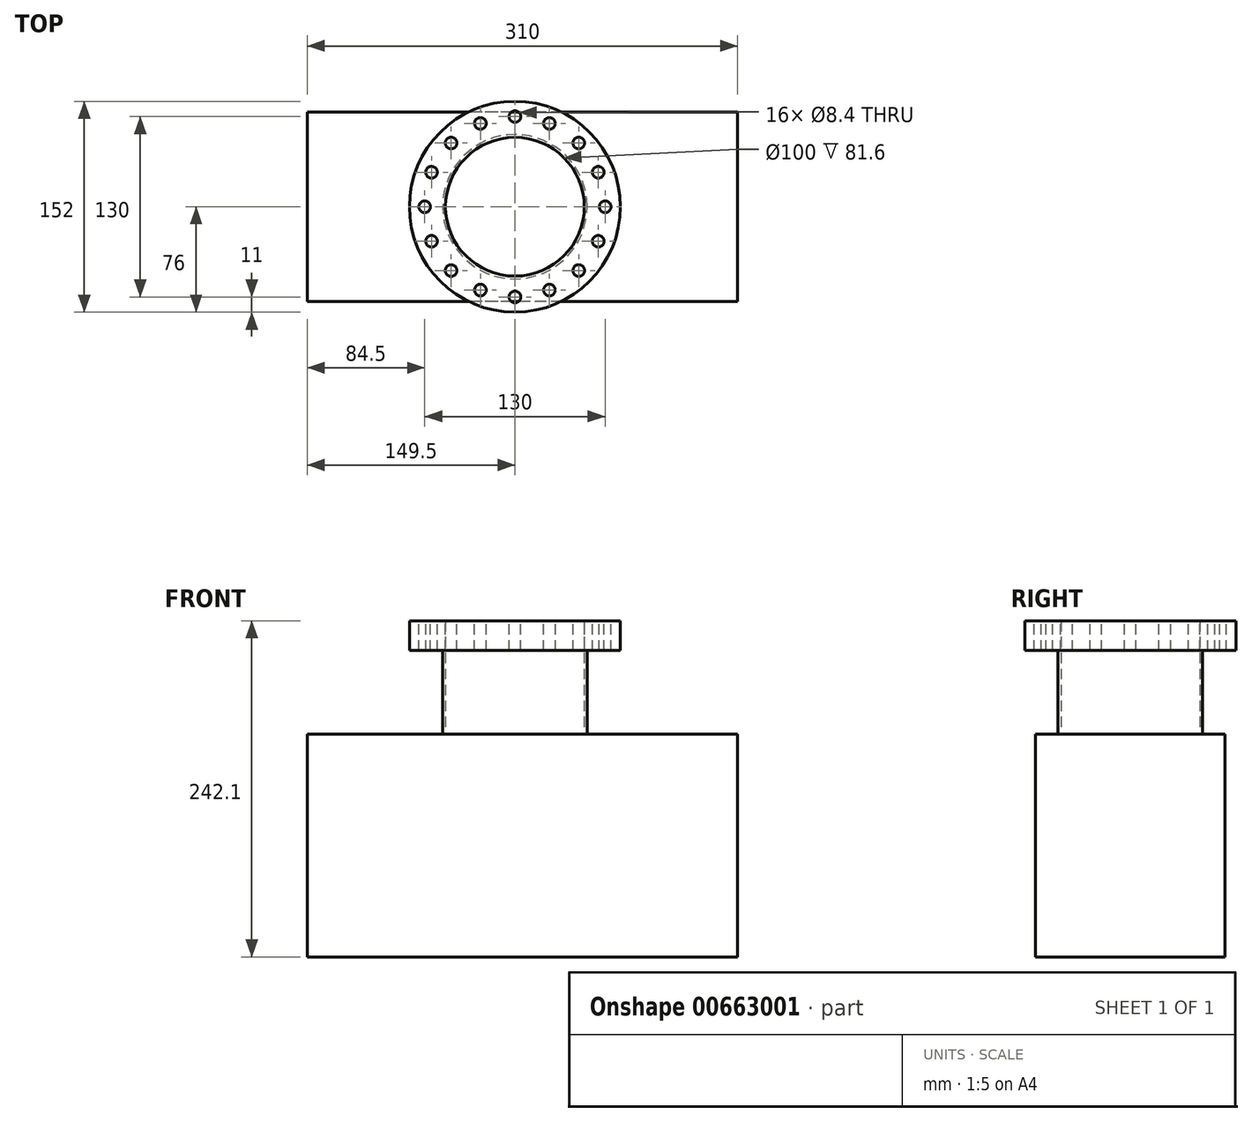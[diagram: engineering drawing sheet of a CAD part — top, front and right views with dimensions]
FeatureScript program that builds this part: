
annotation { "Feature Type Name" : "Feature", "Feature Type Description" : "" }
export const myFeature = defineFeature(function(context is Context, id is Id, definition is map)
    precondition{}
    {
        {
            var Q0;
            Q0=qCreatedBy(makeId("Top.planeOp"),FACE);
            var sketch = newSketch(context, id + "F0", { "sketchPlane" : qUnion([Q0])});
            skLineSegment(sketch, "E0.bottom", {"start": v(155, -68.25) * mm, "end": v(-155, -68.25) * mm});
            skLineSegment(sketch, "E0.top", {"start": v(155, 68.25) * mm, "end": v(-155, 68.25) * mm});
            skLineSegment(sketch, "E0.left", {"start": v(155, -68.25) * mm, "end": v(155, 68.25) * mm});
            skLineSegment(sketch, "E0.right", {"start": v(-155, -68.25) * mm, "end": v(-155, 68.25) * mm});
            skPoint(sketch, "E0.middle", {"position": v(0, 0) * mm});
            skSolve(sketch);
        }
        {
            var Q0;
            Q0=makeQuery(id+"F0.imprint","IMPRINT",FACE,{"disambiguationData":[TD([[makeQuery(id+"F0.imprint","IMPRINT",EDGE,{"derivedFrom":sQuery(id+"F0.wireOp",EDGE,"E0.bottom")}),-1.0]])]});
            extrude(context, id + "F1", {"entities" : qUnion([Q0]), "depth" : (242.1 - 81.6) * mm, "offsetDistance" : 25 * mm});
        }
        {
            var Q0;
            Q0=makeQuery(id+"F1.opExtrude","CAP_FACE",FACE,{"disambiguationData":[OSD([sQuery(id+"F0.wireOp",EDGE,"E0.bottom"),sQuery(id+"F0.wireOp",EDGE,"E0.top"),sQuery(id+"F0.wireOp",EDGE,"E0.left"),sQuery(id+"F0.wireOp",EDGE,"E0.right")])],"isStart":false});
            var sketch = newSketch(context, id + "F2", { "sketchPlane" : qUnion([Q0])});
            skCircle(sketch, "E1", {"center": v(-5.5, 0) * mm, "radius": 50 * mm});
            skCircle(sketch, "E2.0", {"center": v(-5.5, 0) * mm, "radius": 52 * mm});
            skCircle(sketch, "E3", {"center": v(-5.5, 0) * mm, "radius": 76 * mm});
            skSolve(sketch);
        }
        {
            var Q0;
            Q0=makeQuery(id+"F2.imprint","IMPRINT",FACE,{"disambiguationData":[TD([[makeQuery(id+"F2.imprint","IMPRINT",EDGE,{"derivedFrom":sQuery(id+"F2.wireOp",EDGE,"E1")}),-1.0]])]});
            extrude(context, id + "F3", {"entities" : qUnion([Q0]), "operationType" : NewBodyOperationType.ADD, "depth" : (81.6 - 21.3) * mm, "offsetDistance" : 25 * mm});
        }
        {
            var Q0;
            Q0=makeQuery(id+"F3.opExtrude","CAP_FACE",FACE,{"disambiguationData":[OSD([sQuery(id+"F2.wireOp",EDGE,"E1"),sQuery(id+"F2.wireOp",EDGE,"E2.0")])],"isStart":false});
            var sketch = newSketch(context, id + "F4", { "sketchPlane" : qUnion([Q0])});
            skCircle(sketch, "E4", {"center": v(-5.5, 0) * mm, "radius": 76 * mm});
            skSolve(sketch);
        }
        {
            var Q0;
            Q0=makeQuery(id+"F4.imprint","IMPRINT",FACE,{"disambiguationData":[TD([[makeQuery(id+"F4.imprint","IMPRINT",EDGE,{"derivedFrom":makeQuery(id+"F3.opExtrude","CAP_EDGE",EDGE,{"disambiguationData":[OSD([sQuery(id+"F2.wireOp",EDGE,"E1")])],"isStart":false})}),-1.0]])]});
            var Q1;
            Q1=makeQuery(id+"F4.imprint","IMPRINT",FACE,{"disambiguationData":[TD([[makeQuery(id+"F4.imprint","IMPRINT",EDGE,{"derivedFrom":sQuery(id+"F4.wireOp",EDGE,"E4")}),1.0]])]});
            extrude(context, id + "F5", {"entities" : qUnion([Q0, Q1]), "operationType" : NewBodyOperationType.ADD, "depth" : 21.3 * mm, "offsetDistance" : 25 * mm});
        }
        {
            var Q0;
            Q0=makeQuery(id+"F5.opExtrude","CAP_FACE",FACE,{"disambiguationData":[OSD([sQuery(id+"F2.wireOp",EDGE,"E1"),sQuery(id+"F4.wireOp",EDGE,"E4")])],"isStart":false});
            var sketch = newSketch(context, id + "F6", { "sketchPlane" : qUnion([Q0])});
            skCircle(sketch, "E5", {"center": v(-5.5, 0) * mm, "radius": 65 * mm, "construction": true});
            skPoint(sketch, "E6", {"position": v(-70.5, 0) * mm});
            skLineSegment(sketch, "E7", {"start": v(-70.5, 0) * mm, "end": v(-5.5, 0) * mm, "construction": true});
            skPoint(sketch, "E8.1.0", {"position": v(-65.55, -24.87) * mm});
            skPoint(sketch, "E8.2.0", {"position": v(-51.46, -45.96) * mm});
            skPoint(sketch, "E8.3.0", {"position": v(-30.37, -60.05) * mm});
            skPoint(sketch, "E8.4.0", {"position": v(-5.5, -65) * mm});
            skPoint(sketch, "E8.5.0", {"position": v(19.37, -60.05) * mm});
            skPoint(sketch, "E8.6.0", {"position": v(40.46, -45.96) * mm});
            skPoint(sketch, "E8.7.0", {"position": v(54.55, -24.87) * mm});
            skPoint(sketch, "E8.8.0", {"position": v(59.5, 0) * mm});
            skPoint(sketch, "E8.9.0", {"position": v(54.55, 24.87) * mm});
            skPoint(sketch, "E8.10.0", {"position": v(40.46, 45.96) * mm});
            skPoint(sketch, "E8.11.0", {"position": v(19.37, 60.05) * mm});
            skPoint(sketch, "E8.12.0", {"position": v(-5.5, 65) * mm});
            skPoint(sketch, "E8.13.0", {"position": v(-30.37, 60.05) * mm});
            skPoint(sketch, "E8.14.0", {"position": v(-51.46, 45.96) * mm});
            skPoint(sketch, "E8.15.0", {"position": v(-65.55, 24.87) * mm});
            skSolve(sketch);
        }
        {
            var Q0;
            Q0=sQuery(id+"F6.wireOp",VERTEX,"E8.12.0");
            var Q1;
            Q1=sQuery(id+"F6.wireOp",VERTEX,"E8.11.0");
            var Q2;
            Q2=sQuery(id+"F6.wireOp",VERTEX,"E8.10.0");
            var Q3;
            Q3=sQuery(id+"F6.wireOp",VERTEX,"E8.9.0");
            var Q4;
            Q4=sQuery(id+"F6.wireOp",VERTEX,"E8.8.0");
            var Q5;
            Q5=sQuery(id+"F6.wireOp",VERTEX,"E8.7.0");
            var Q6;
            Q6=sQuery(id+"F6.wireOp",VERTEX,"E8.6.0");
            var Q7;
            Q7=sQuery(id+"F6.wireOp",VERTEX,"E8.5.0");
            var Q8;
            Q8=sQuery(id+"F6.wireOp",VERTEX,"E8.4.0");
            var Q9;
            Q9=sQuery(id+"F6.wireOp",VERTEX,"E8.3.0");
            var Q10;
            Q10=sQuery(id+"F6.wireOp",VERTEX,"E8.2.0");
            var Q11;
            Q11=sQuery(id+"F6.wireOp",VERTEX,"E8.1.0");
            var Q12;
            Q12=sQuery(id+"F6.wireOp",VERTEX,"E6");
            var Q13;
            Q13=sQuery(id+"F6.wireOp",VERTEX,"E8.15.0");
            var Q14;
            Q14=sQuery(id+"F6.wireOp",VERTEX,"E8.14.0");
            var Q15;
            Q15=sQuery(id+"F6.wireOp",VERTEX,"E8.13.0");
            var Q16;
            Q16=makeQuery(id+"F1.opExtrude","SWEPT_BODY",BODY,{"disambiguationData":[OSD([sQuery(id+"F0.wireOp",EDGE,"E0.bottom"),sQuery(id+"F0.wireOp",EDGE,"E0.top"),sQuery(id+"F0.wireOp",EDGE,"E0.left"),sQuery(id+"F0.wireOp",EDGE,"E0.right")])]});
            hole(context, id + "F7", {"style" : HoleStyle.SIMPLE, "endStyle" : HoleEndStyle.BLIND, "standardTappedOrClearance" : lookupTablePath({ "fit" : "Close", "standard" : "ISO", "size" : "M8", "type" : "Clearance" }), "standardBlindInLast" : lookupTablePath({ "fit" : "Close", "standard" : "ISO", "engagement" : "75%", "pitch" : "1.25 mm", "size" : "M8", "type" : "Clearance & tapped" }), "holeDiameter" : 8.4 * mm, "majorDiameter" : 5 * mm, "holeDepth" : 24 * mm, "isTappedThrough" : true, "tappedDepth" : 12 * mm, "tapClearance" : 3, "locations" : qUnion([Q0, Q1, Q2, Q3, Q4, Q5, Q6, Q7, Q8, Q9, Q10, Q11, Q12, Q13, Q14, Q15]), "scope" : qUnion([Q16])});
        }
    });
